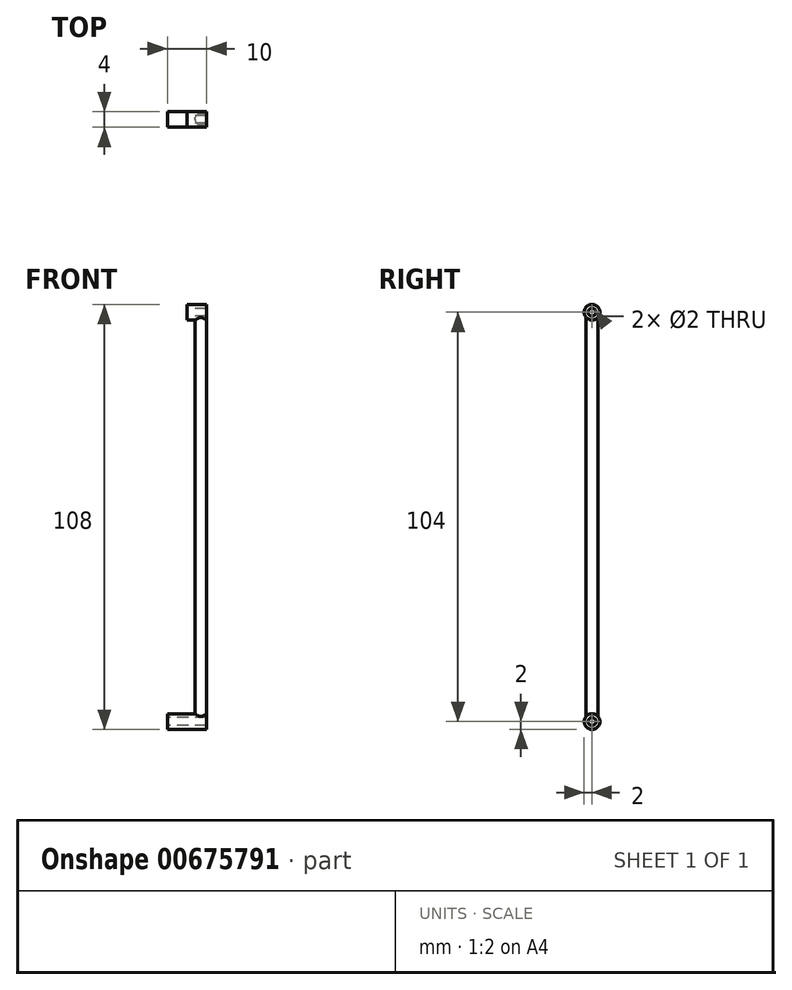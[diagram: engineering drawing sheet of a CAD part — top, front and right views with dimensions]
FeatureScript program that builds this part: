
annotation { "Feature Type Name" : "Feature", "Feature Type Description" : "" }
export const myFeature = defineFeature(function(context is Context, id is Id, definition is map)
    precondition{}
    {
        {
            var Q0;
            Q0=qCreatedBy(makeId("Top.planeOp"),FACE);
            var sketch = newSketch(context, id + "F0", { "sketchPlane" : qUnion([Q0])});
            skCircle(sketch, "E0", {"center": v(0, 0) * mm, "radius": 1.5 * mm});
            skSolve(sketch);
        }
        {
            var Q0;
            Q0=makeQuery(id+"F0.imprint","IMPRINT",FACE,{"disambiguationData":[TD([[makeQuery(id+"F0.imprint","IMPRINT",EDGE,{"derivedFrom":sQuery(id+"F0.wireOp",EDGE,"E0")}),1.0]])]});
            extrude(context, id + "F1", {"entities" : qUnion([Q0]), "depth" : 100 * mm, "offsetDistance" : 25 * mm, "hasSecondDirection" : true, "secondDirectionOppositeDirection" : true, "secondDirectionDepth" : 0.75 * mm});
        }
        {
            var Q0;
            Q0=qCreatedBy(makeId("Front.planeOp"),FACE);
            var sketch = newSketch(context, id + "F2", { "sketchPlane" : qUnion([Q0])});
            skLineSegment(sketch, "E1", {"start": v(-5, 0) * mm, "end": v(-5, 0) * mm});
            skLineSegment(sketch, "E2", {"start": v(0, -2) * mm, "end": v(2.33, -2) * mm});
            skLineSegment(sketch, "E3", {"start": v(1.5, 0) * mm, "end": v(1.5, -1) * mm});
            skLineSegment(sketch, "E4", {"start": v(-8.5, -1) * mm, "end": v(-8.5, 0) * mm});
            skLineSegment(sketch, "E5", {"start": v(1.5, 0) * mm, "end": v(-8.5, 0) * mm});
            skLineSegment(sketch, "E6", {"start": v(1.5, -1) * mm, "end": v(-8.5, -1) * mm});
            skLineSegment(sketch, "E7", {"start": v(1.5, 100) * mm, "end": v(1.5, 101) * mm});
            skLineSegment(sketch, "E8", {"start": v(-3.5, 101) * mm, "end": v(-3.5, 100) * mm});
            skLineSegment(sketch, "E9", {"start": v(-3.5, 100) * mm, "end": v(1.5, 100) * mm});
            skLineSegment(sketch, "E10", {"start": v(-3.5, 101) * mm, "end": v(1.5, 101) * mm});
            skLineSegment(sketch, "E11.MirrorCS", {"start": v(0, 102) * mm, "end": v(2.33, 102) * mm});
            skSolve(sketch);
        }
        {
            var Q0;
            Q0=makeQuery(id+"F2.imprint","IMPRINT",FACE,{"disambiguationData":[TD([[makeQuery(id+"F2.imprint","IMPRINT",EDGE,{"derivedFrom":sQuery(id+"F2.wireOp",EDGE,"E3")}),-1.0]])]});
            var Q1;
            Q1=sQuery(id+"F2.wireOp",EDGE,"E2");
            revolve(context, id + "F3", {"operationType" : NewBodyOperationType.ADD, "entities" : qUnion([Q0]), "axis" : qUnion([Q1]), "revolveType" : RevolveType.FULL});
        }
        {
            var Q0;
            Q0=makeQuery(id+"F2.imprint","IMPRINT",FACE,{"disambiguationData":[TD([[makeQuery(id+"F2.imprint","IMPRINT",EDGE,{"derivedFrom":sQuery(id+"F2.wireOp",EDGE,"E7")}),1.0]])]});
            var Q1;
            Q1=sQuery(id+"F2.wireOp",EDGE,"E11.MirrorCS");
            revolve(context, id + "F4", {"operationType" : NewBodyOperationType.ADD, "entities" : qUnion([Q0]), "axis" : qUnion([Q1]), "revolveType" : RevolveType.FULL});
        }
        {
            var Q0;
            Q0=makeQuery(id+"F1.opExtrude","CAP_FACE",FACE,{"disambiguationData":[OSD([sQuery(id+"F0.wireOp",EDGE,"E0")])],"isStart":false});
            extrude(context, id + "F5", {"entities" : qUnion([Q0]), "operationType" : NewBodyOperationType.ADD, "depth" : 1 * mm, "offsetDistance" : 25 * mm});
        }
    });
